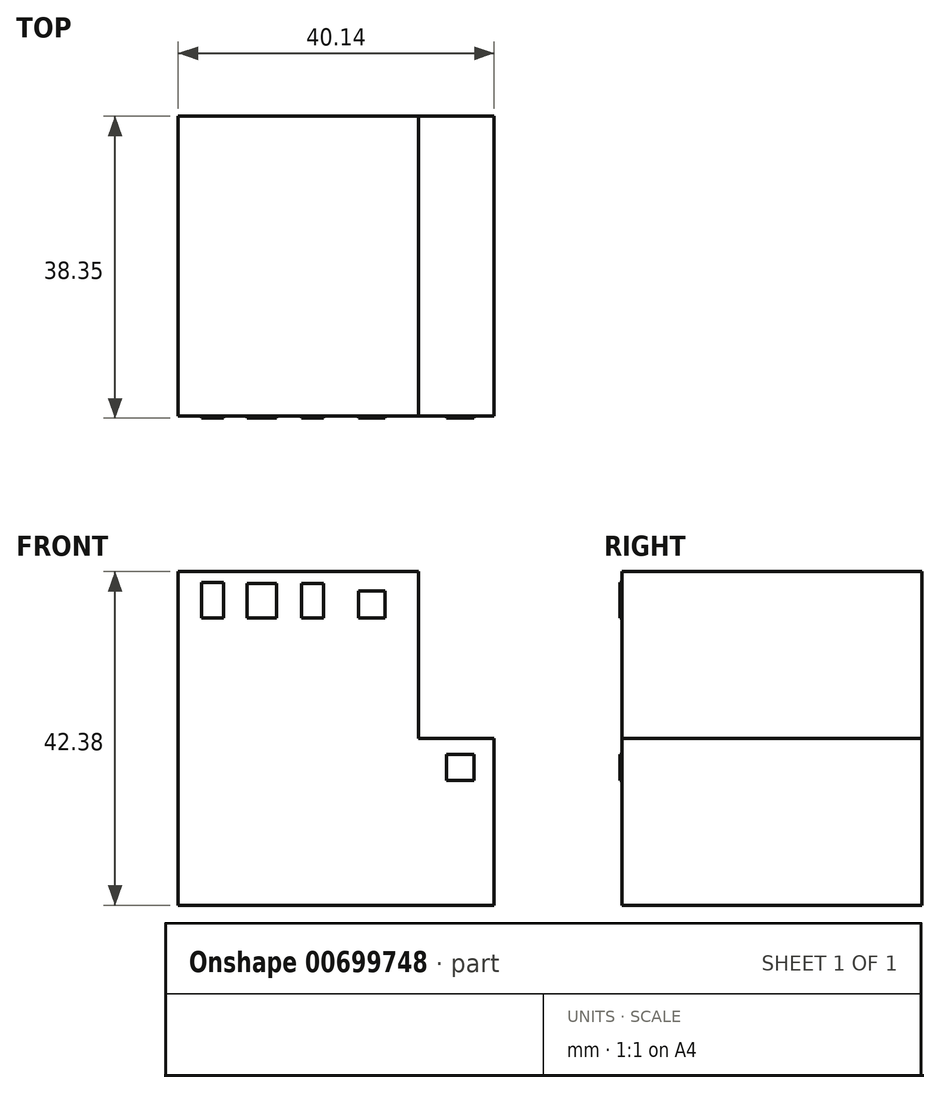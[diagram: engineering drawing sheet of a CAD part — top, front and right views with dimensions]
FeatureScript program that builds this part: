
annotation { "Feature Type Name" : "Feature", "Feature Type Description" : "" }
export const myFeature = defineFeature(function(context is Context, id is Id, definition is map)
    precondition{}
    {
        {
            var Q0;
            Q0=qCreatedBy(makeId("Front.planeOp"),FACE);
            var sketch = newSketch(context, id + "F0", { "sketchPlane" : qUnion([Q0])});
            skLineSegment(sketch, "E0.bottom", {"start": v(-115.74, 24.1) * mm, "end": v(-85.23, 24.1) * mm});
            skLineSegment(sketch, "E0.top", {"start": v(-115.74, -18.3) * mm, "end": v(-85.23, -18.3) * mm});
            skLineSegment(sketch, "E0.left", {"start": v(-115.74, 24.1) * mm, "end": v(-115.74, -18.3) * mm});
            skLineSegment(sketch, "E0.right", {"start": v(-85.23, 24.1) * mm, "end": v(-85.23, -18.3) * mm});
            skPoint(sketch, "E1.oppositeSnap0", {"position": v(-85.23, 2.9) * mm});
            skLineSegment(sketch, "E1.bottom", {"start": v(-85.23, 2.9) * mm, "end": v(-75.6, 2.9) * mm});
            skLineSegment(sketch, "E1.top", {"start": v(-85.23, 2.9) * mm, "end": v(-75.6, 2.9) * mm});
            skLineSegment(sketch, "E1.left", {"start": v(-85.23, 2.9) * mm, "end": v(-85.23, 2.9) * mm});
            skLineSegment(sketch, "E1.right", {"start": v(-75.6, 2.9) * mm, "end": v(-75.6, 2.9) * mm});
            skLineSegment(sketch, "E2.top", {"start": v(-75.6, -18.3) * mm, "end": v(-75.6, -18.3) * mm});
            skLineSegment(sketch, "E2.left", {"start": v(-75.6, 2.9) * mm, "end": v(-75.6, -18.3) * mm});
            skLineSegment(sketch, "E2.right", {"start": v(-75.6, 2.9) * mm, "end": v(-75.6, -18.3) * mm});
            skLineSegment(sketch, "E3.bottom", {"start": v(-75.6, -18.3) * mm, "end": v(-85.23, -18.3) * mm});
            skLineSegment(sketch, "E3.top", {"start": v(-75.6, -18.3) * mm, "end": v(-85.23, -18.3) * mm});
            skLineSegment(sketch, "E3.right", {"start": v(-85.23, -18.3) * mm, "end": v(-85.23, -18.3) * mm});
            skSolve(sketch);
        }
        {
            var Q0;
            Q0 = qSketchRegion(id + "F0", true);
            extrude(context, id + "F1", {"entities" : qUnion([Q0]), "depth" : 12.7 * mm, "offsetDistance" : 25.4 * mm});
        }
        {
            var Q0;
            Q0=makeQuery(id+"F1.opExtrude","CAP_FACE",FACE,{"disambiguationData":[OSD([sQuery(id+"F0.wireOp",EDGE,"E0.bottom"),sQuery(id+"F0.wireOp",EDGE,"E0.top"),sQuery(id+"F0.wireOp",EDGE,"E0.left"),sQuery(id+"F0.wireOp",EDGE,"E0.right"),sQuery(id+"F0.wireOp",EDGE,"E1.top"),sQuery(id+"F0.wireOp",EDGE,"E2.right"),sQuery(id+"F0.wireOp",EDGE,"E3.top")])],"isStart":false});
            extrude(context, id + "F2", {"entities" : qUnion([Q0]), "operationType" : NewBodyOperationType.ADD, "depth" : 25.4 * mm, "offsetDistance" : 25.4 * mm});
        }
        {
            var Q0;
            Q0=makeQuery(id+"F2.opExtrude","CAP_FACE",FACE,{"disambiguationData":[OSD([sQuery(id+"F0.wireOp",EDGE,"E0.bottom"),sQuery(id+"F0.wireOp",EDGE,"E0.top"),sQuery(id+"F0.wireOp",EDGE,"E0.left"),sQuery(id+"F0.wireOp",EDGE,"E0.right"),sQuery(id+"F0.wireOp",EDGE,"E1.top"),sQuery(id+"F0.wireOp",EDGE,"E2.right"),sQuery(id+"F0.wireOp",EDGE,"E3.top")])],"isStart":false});
            var sketch = newSketch(context, id + "F3", { "sketchPlane" : qUnion([Q0])});
            skLineSegment(sketch, "E4.bottom", {"start": v(-112.74, 22.74) * mm, "end": v(-110, 22.74) * mm});
            skLineSegment(sketch, "E4.top", {"start": v(-112.74, 18.21) * mm, "end": v(-110, 18.21) * mm});
            skLineSegment(sketch, "E4.left", {"start": v(-112.74, 22.74) * mm, "end": v(-112.74, 18.21) * mm});
            skLineSegment(sketch, "E4.right", {"start": v(-110, 22.74) * mm, "end": v(-110, 18.21) * mm});
            skLineSegment(sketch, "E5.bottom", {"start": v(-106.99, 22.58) * mm, "end": v(-103.27, 22.58) * mm});
            skLineSegment(sketch, "E5.top", {"start": v(-106.99, 18.21) * mm, "end": v(-103.27, 18.21) * mm});
            skLineSegment(sketch, "E5.left", {"start": v(-106.99, 22.58) * mm, "end": v(-106.99, 18.21) * mm});
            skLineSegment(sketch, "E5.right", {"start": v(-103.27, 22.58) * mm, "end": v(-103.27, 18.21) * mm});
            skLineSegment(sketch, "E6.bottom", {"start": v(-100.05, 22.59) * mm, "end": v(-97.28, 22.59) * mm});
            skLineSegment(sketch, "E6.top", {"start": v(-100.05, 18.21) * mm, "end": v(-97.28, 18.21) * mm});
            skLineSegment(sketch, "E6.left", {"start": v(-100.05, 22.59) * mm, "end": v(-100.05, 18.21) * mm});
            skLineSegment(sketch, "E6.right", {"start": v(-97.28, 22.59) * mm, "end": v(-97.28, 18.21) * mm});
            skLineSegment(sketch, "E7.bottom", {"start": v(-92.83, 21.66) * mm, "end": v(-89.45, 21.66) * mm});
            skLineSegment(sketch, "E7.top", {"start": v(-92.83, 18.21) * mm, "end": v(-89.45, 18.21) * mm});
            skLineSegment(sketch, "E7.left", {"start": v(-92.83, 21.66) * mm, "end": v(-92.83, 18.21) * mm});
            skLineSegment(sketch, "E7.right", {"start": v(-89.45, 21.66) * mm, "end": v(-89.45, 18.21) * mm});
            skLineSegment(sketch, "E8.bottom", {"start": v(-78.2, 0.9) * mm, "end": v(-81.67, 0.9) * mm});
            skLineSegment(sketch, "E8.top", {"start": v(-78.2, -2.42) * mm, "end": v(-81.67, -2.42) * mm});
            skLineSegment(sketch, "E8.left", {"start": v(-78.2, 0.9) * mm, "end": v(-78.2, -2.42) * mm});
            skLineSegment(sketch, "E8.right", {"start": v(-81.67, 0.9) * mm, "end": v(-81.67, -2.42) * mm});
            skSolve(sketch);
        }
        {
            var Q0;
            Q0=makeQuery(id+"F3.imprint","IMPRINT",FACE,{"disambiguationData":[TD([[makeQuery(id+"F3.imprint","IMPRINT",EDGE,{"derivedFrom":sQuery(id+"F3.wireOp",EDGE,"E7.bottom")}),-1.0]])]});
            var sketch = newSketch(context, id + "F4", { "sketchPlane" : qUnion([Q0])});
            skSolve(sketch);
        }
        {
            var Q0;
            Q0=makeQuery(id+"F4.imprint","IMPRINT",FACE,{"disambiguationData":[TD([[makeQuery(id+"F4.imprint","IMPRINT",EDGE,{"derivedFrom":makeQuery(id+"F3.imprint","IMPRINT",EDGE,{"derivedFrom":sQuery(id+"F3.wireOp",EDGE,"E7.bottom")})}),-1.0]])]});
            var Q1;
            Q1=makeQuery(id+"F3.imprint","IMPRINT",FACE,{"disambiguationData":[TD([[makeQuery(id+"F3.imprint","IMPRINT",EDGE,{"derivedFrom":sQuery(id+"F3.wireOp",EDGE,"E6.bottom")}),-1.0]])]});
            var Q2;
            Q2=makeQuery(id+"F3.imprint","IMPRINT",FACE,{"disambiguationData":[TD([[makeQuery(id+"F3.imprint","IMPRINT",EDGE,{"derivedFrom":sQuery(id+"F3.wireOp",EDGE,"E5.bottom")}),-1.0]])]});
            var Q3;
            Q3=makeQuery(id+"F3.imprint","IMPRINT",FACE,{"disambiguationData":[TD([[makeQuery(id+"F3.imprint","IMPRINT",EDGE,{"derivedFrom":sQuery(id+"F3.wireOp",EDGE,"E4.bottom")}),-1.0]])]});
            var Q4;
            Q4=makeQuery(id+"F3.imprint","IMPRINT",FACE,{"disambiguationData":[TD([[makeQuery(id+"F3.imprint","IMPRINT",EDGE,{"derivedFrom":sQuery(id+"F3.wireOp",EDGE,"E8.bottom")}),1.0]])]});
            extrude(context, id + "F5", {"entities" : qUnion([Q0, Q1, Q2, Q3, Q4]), "operationType" : NewBodyOperationType.ADD, "depth" : 0.25 * mm, "offsetDistance" : 25.4 * mm});
        }
    });
